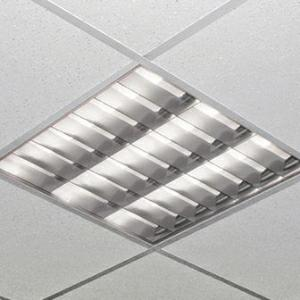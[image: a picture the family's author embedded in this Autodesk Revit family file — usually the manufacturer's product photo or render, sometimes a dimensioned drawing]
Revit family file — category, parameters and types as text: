
# Revit family: 3f_filippi_-_l_320_2s_3f_filippi_-_28826_-_l_323x10w_led_2s_596x596
name_source: partatom
category: Lighting Fixtures
units: mm (PartAtom-declared; Revit-internal decimal feet)

## family parameters
Cut with Voids When Loaded = No
Host = Face
Light Source = No
Part Type = Normal
Room Calculation Point = No
Round Connector Dimension = Use Diameter
Shared = No

## types (1)
- 3F Filippi - L 320 2S (1 x LED, 3997 lm, 34 W, 4000 K)
    Apparent Load = 34 VA
    Approval mark = ENEC
    CIE Flux Codes = 71 98 100 100 100
    Color Rendering = 80
    Color Temperature = 4000 K
    Control Gear = Electronic ballast
    Default Elevation = 1800 mm
    Description = ILLUMINOTECHNICAL
Luminous efficiency 100% (DLOR 100%, ULOR 0%).
Initial luminous flux of the luminaire 3997 lm.
Direct symmetric distribution.
Installation Interdistance Transv.D = 1.21 x hu - Long.D = 1.14 x hu.
Average luminance <1000 cd/m² for radial angles >65°.
Tabular UGR (CIE 117 - 4H-8H; S=0.25H; 70/50/20): RUG 14.7 - 15.3.
Beam angle: 87° - 86°.
Luminous efficacy 118 lm/W.
Lifetime (L93/B10): 30000 h. (tq+25°C)
Lifetime (L90/B10): 50000 h. (tq+25°C)
Lifetime (L85/B10): 80000 h. (tq+25°C)
Lifetime (L80/B10): 100000 h. (tq+25°C)
Sudden decreased luminous flux after 50000 hours: 0% (C0).
Photobiological safety in compliance with IEC/TR 62778: RG0 risk exempt, (IEC 62471).
In compliance with IEC/EN 62722-2-1 - IEC/EN 62717 standards.

SOURCE
3 linear LED modules 10W/840.
Energy efficiency class (UE 2019/2020 - UE 2019/2015): D.
CIE 13.3 Colour rendering index: CRI >80 (R9 <50%).
IES TM-30 Fidelity Index: Rf = 84 Rg = 95.
CCT nominal colour temperature 4000 K.
Colour initial tolerance (MacAdam): SDCM 2.

MECHANICAL
Housing in hot-galvanised steel, painted in white polyester.
2S parabolic louvre in semi-specular aluminium, non-reflecting, with transverse blades closed at the top.
Prismatic flat diffusers in transparent methacrylate (PMMA), multilenticular, anti-glare, prismatic outer surface, positioned above the louvre blades.
Film protective against dust and finger marks, adhesive, attached to louvre.
Luminaire with limited surface temperature. - D - (EN 60598-2-24)
Dimensions: 596x596 mm, height 80 mm. Weight 4.23 kg.
IP20 protection degree.
Mechanical strength to impacts IK02 (0.2 joule).
Glow-wire test resistance 650°C.

ELECTRICAL
Halogen Free electronic wiring 230V-50/60Hz, power factor 0.90, THD <25%, constant output current, SELV, class I, 1 driver.
Power of the luminaire 34 W.
CE - IEC 60598-1 - EN 60598-1.
SAFE FLICKER: PstLM=<1 and SVM=<0.4 (IEC TR 61547-1 and IEC TR 63158), to ensure a more comfortable and safe light.
Luminaire compliant with EN 60598-2-22 for power supply from a centralised emergency system CPSS (Central Power Supply System), not incorporated in the luminaire - high risk areas excluded. The default power and flux are 100% in AC and 100% in DC.
Ambient temperature from 0°C to +25°C.
Temperature class T6 max 85°C.
Relative humidity UR: <85%.

INSTALLATION
Lay-in recessed fitting.
On request: pull-up recessed fitting with brackets.
False ceiling carving: 580x580 mm.
All accessories dedicated to this product are available on the Catalog and on our website www.3F-Filippi.com.

APPLICATIONS
In environments with VDTs, managerial offices and staterooms, public offices and schools.

WARNING
Luminaire designed for disposal/recycling at end-of-life.
Replaceable (LED only) light source by a professional. Replaceable control gear by a professional.
    Height = 0 mm  [stored 0 ft]
    Lamp = 1 x LED
    Lamp Light Flux = 3997 lm
    Lamp Power = 34 W
    Lamp count = 1
    Length = 596 mm
    Lifetime = 50000 h
    Luminous efficacy = 118 lm/W
    Manufacturer = 3F Filippi
    ModVariant = No
    Model = 3F Filippi - 28826 - L 323x10W LED 2S 596x596
    Mounting Place = Ceiling
    Mounting Type = Recessed
    Number of Poles = 1
    OnlyDefault = Yes
    Power Factor = 1
    Product Name = 3F Filippi - L 320 2S
    Product group = recessed luminaire
    ProductGroupID = 4
    Protection Class = Protection class I
    Protection Degree = IP 20
    RLX_Detail_Level = 1
    RLX_Emergency_Light_Flux = 0 lm
    RLX_Emergency_Type = 0
    RLX_Emergency_Type_DB = No
    RlxData = <blob elided: 92921 chars, md5=daa68906>
    Socket = socket
    Standby Power = 0 W
    System Light Flux = 3997 lm
    System Power = 34 W
    Type Comments = Product without accessories
    Type Image = 3ffilippi_28826.jpg
    URL = http://relux.com
    VarID = ---
    Voltage = 0 V
    Weight = 0.00 kg
    Width = 596 mm

note: [stored X ft] marks values corroborated as IEEE doubles in the binary element streams (Revit-internal decimal feet)

## geometry (parser evidence)
native form markers: Blend x4, Sweep x11
no freeform markers — native parametric forms only
